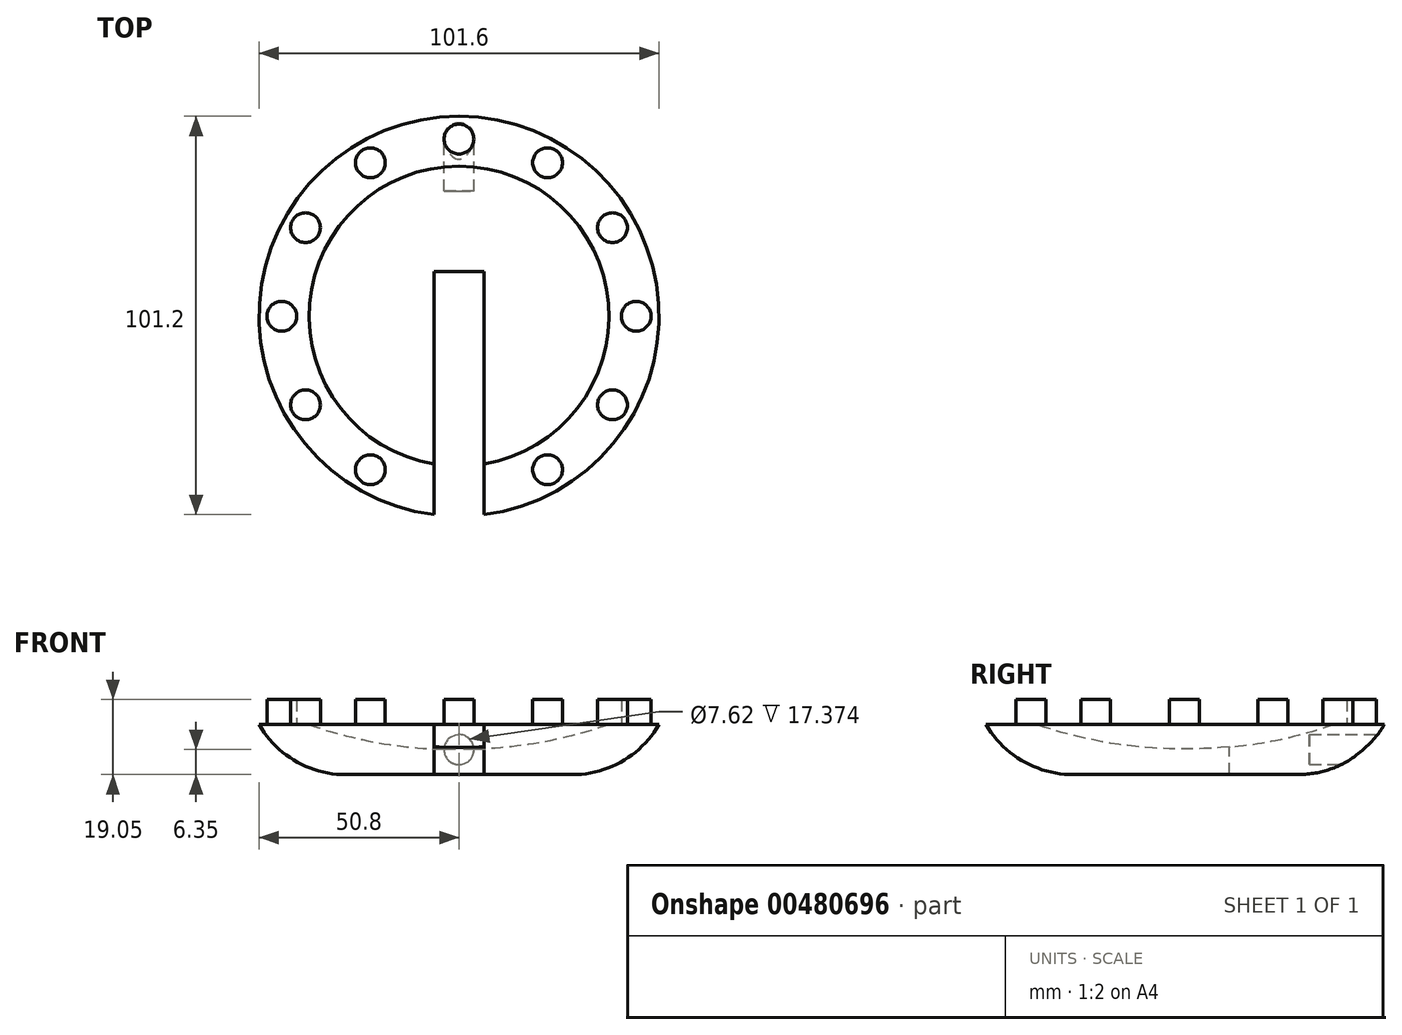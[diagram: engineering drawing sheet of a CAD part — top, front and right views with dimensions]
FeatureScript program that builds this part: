
annotation { "Feature Type Name" : "Feature", "Feature Type Description" : "" }
export const myFeature = defineFeature(function(context is Context, id is Id, definition is map)
    precondition{}
    {
        {
            var Q0;
            Q0=qCreatedBy(makeId("Top.planeOp"),FACE);
            var sketch = newSketch(context, id + "F0", { "sketchPlane" : qUnion([Q0])});
            skCircle(sketch, "E0", {"center": v(0, 0) * mm, "radius": 50.8 * mm});
            skSolve(sketch);
        }
        {
            var Q0;
            Q0 = qSketchRegion(id + "F0", true);
            extrude(context, id + "F1", {"entities" : qUnion([Q0]), "depth" : 12.7 * mm});
        }
        {
            var Q0;
            Q0=makeQuery(id+"F1.opExtrude","CAP_EDGE",EDGE,{"disambiguationData":[OSD([sQuery(id+"F0.wireOp",EDGE,"E0")])],"isStart":true});
            fillet(context, id + "F2", {"entities" : qUnion([Q0]), "radius" : 25.4 * mm, "tangentPropagation" : true, "allowEdgeOverflow" : false});
        }
        {
            var Q0;
            Q0=makeQuery(id+"F1.opExtrude","CAP_FACE",FACE,{"disambiguationData":[OSD([sQuery(id+"F0.wireOp",EDGE,"E0")])],"isStart":false});
            var sketch = newSketch(context, id + "F3", { "sketchPlane" : qUnion([Q0])});
            skCircle(sketch, "E1", {"center": v(0, 0) * mm, "radius": 38.1 * mm});
            skSolve(sketch);
        }
        {
            var Q0;
            Q0 = qSketchRegion(id + "F3", true);
            extrude(context, id + "F4", {"entities" : qUnion([Q0]), "operationType" : NewBodyOperationType.REMOVE, "oppositeDirection" : true, "depth" : 6.35 * mm});
        }
        {
            var Q0;
            Q0=makeQuery(id+"F4.boolean.opBoolean","COPY",EDGE,{"derivedFrom":makeQuery(id+"F4.opExtrude","CAP_EDGE",EDGE,{"disambiguationData":[OSD([sQuery(id+"F3.wireOp",EDGE,"E1")])],"isStart":false})});
            fillet(context, id + "F5", {"entities" : qUnion([Q0]), "radius" : 114.3 * mm, "tangentPropagation" : true, "allowEdgeOverflow" : false});
        }
        {
            var Q0;
            Q0=makeQuery(id+"F1.opExtrude","CAP_FACE",FACE,{"disambiguationData":[OSD([sQuery(id+"F0.wireOp",EDGE,"E0")])],"isStart":false});
            var sketch = newSketch(context, id + "F6", { "sketchPlane" : qUnion([Q0])});
            skLineSegment(sketch, "E2.bottom", {"start": v(-6.35, -72.46) * mm, "end": v(6.35, -72.46) * mm});
            skLineSegment(sketch, "E2.top", {"start": v(-6.35, 11.41) * mm, "end": v(6.35, 11.41) * mm});
            skLineSegment(sketch, "E2.left", {"start": v(-6.35, -72.46) * mm, "end": v(-6.35, 11.41) * mm});
            skLineSegment(sketch, "E2.right", {"start": v(6.35, -72.46) * mm, "end": v(6.35, 11.41) * mm});
            skSolve(sketch);
        }
        {
            var Q0;
            Q0 = qSketchRegion(id + "F6", true);
            extrude(context, id + "F7", {"entities" : qUnion([Q0]), "operationType" : NewBodyOperationType.REMOVE, "oppositeDirection" : true, "depth" : 25.4 * mm});
        }
        {
            var Q0;
            Q0=qCreatedBy(makeId("Front.planeOp"),FACE);
            cPlane(context, id + "F8", {"entities" : qUnion([Q0]), "cplaneType" : CPlaneType.OFFSET, "offset" : 73.4 * mm, "oppositeDirection" : true, "width" : 152.4 * mm, "height" : 152.4 * mm});
        }
        {
            var Q0;
            Q0=qCreatedBy(id+"F8.planeOp",FACE);
            var sketch = newSketch(context, id + "F9", { "sketchPlane" : qUnion([Q0])});
            skCircle(sketch, "E3", {"center": v(0, 6.35) * mm, "radius": 3.81 * mm});
            skSolve(sketch);
        }
        {
            var Q0;
            Q0 = qSketchRegion(id + "F9", true);
            extrude(context, id + "F10", {"entities" : qUnion([Q0]), "operationType" : NewBodyOperationType.REMOVE, "depth" : 41.66 * mm});
        }
        {
            var Q0;
            Q0=makeQuery(id+"F1.opExtrude","CAP_FACE",FACE,{"disambiguationData":[OSD([sQuery(id+"F0.wireOp",EDGE,"E0")])],"isStart":false});
            var sketch = newSketch(context, id + "F11", { "sketchPlane" : qUnion([Q0])});
            skCircle(sketch, "E4", {"center": v(-45.03, 0) * mm, "radius": 3.78 * mm});
            skCircle(sketch, "E5.1.0", {"center": v(-39, -22.51) * mm, "radius": 3.78 * mm});
            skCircle(sketch, "E5.2.0", {"center": v(-22.51, -39) * mm, "radius": 3.78 * mm});
            skPoint(sketch, "E5.center", {"position": v(0, 0) * mm});
            skCircle(sketch, "E6.1.4.0", {"center": v(22.51, -39) * mm, "radius": 3.78 * mm});
            skCircle(sketch, "E6.1.5.0", {"center": v(39, -22.51) * mm, "radius": 3.78 * mm});
            skCircle(sketch, "E6.1.6.0", {"center": v(45.03, 0) * mm, "radius": 3.78 * mm});
            skCircle(sketch, "E6.1.7.0", {"center": v(39, 22.51) * mm, "radius": 3.78 * mm});
            skCircle(sketch, "E6.1.8.0", {"center": v(22.51, 39) * mm, "radius": 3.78 * mm});
            skCircle(sketch, "E6.1.9.0", {"center": v(0, 45.03) * mm, "radius": 3.78 * mm});
            skCircle(sketch, "E6.1.10.0", {"center": v(-22.51, 39) * mm, "radius": 3.78 * mm});
            skCircle(sketch, "E6.1.11.0", {"center": v(-39, 22.51) * mm, "radius": 3.78 * mm});
            skSolve(sketch);
        }
        {
            var Q0;
            Q0 = qSketchRegion(id + "F11", true);
            extrude(context, id + "F12", {"entities" : qUnion([Q0]), "operationType" : NewBodyOperationType.ADD, "depth" : 6.35 * mm, "offsetDistance" : 25.4 * mm});
        }
    });
